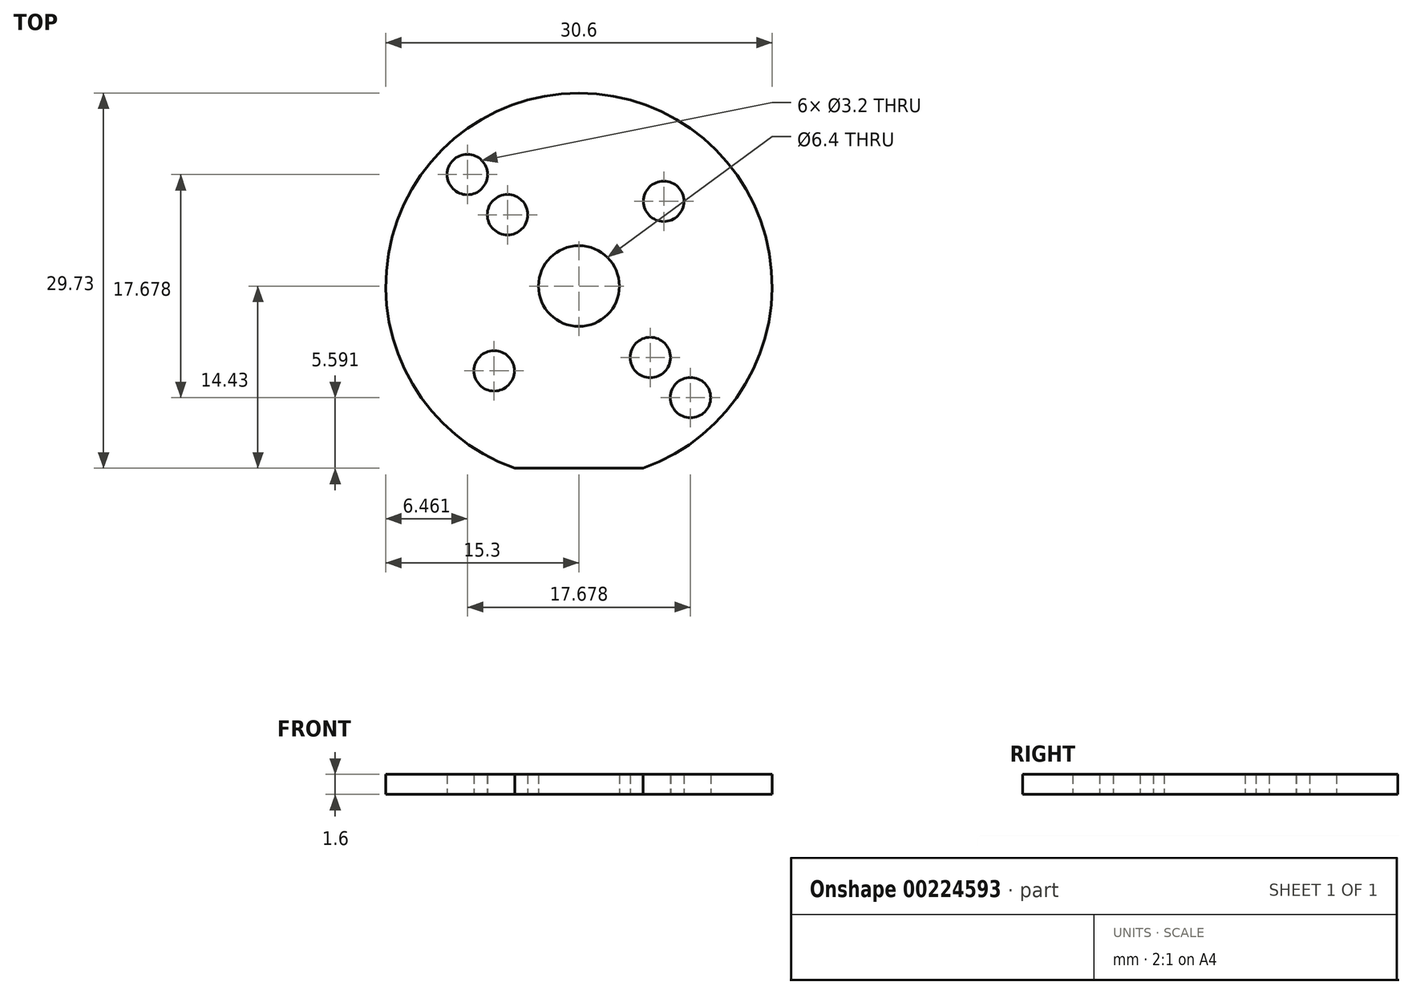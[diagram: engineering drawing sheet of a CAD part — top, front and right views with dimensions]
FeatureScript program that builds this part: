
annotation { "Feature Type Name" : "Feature", "Feature Type Description" : "" }
export const myFeature = defineFeature(function(context is Context, id is Id, definition is map)
    precondition{}
    {
        {
            var Q0;
            Q0=qCreatedBy(makeId("Top.planeOp"),FACE);
            var sketch = newSketch(context, id + "F0", { "sketchPlane" : qUnion([Q0])});
            skLineSegment(sketch, "E0", {"start": v(5.08, -14.43) * mm, "end": v(-5.08, -14.43) * mm});
            skArc(sketch, "E1", {"start": v(5.08, -14.43) * mm, "mid": v(0, 15.3) * mm, "end": v(-5.08, -14.43) * mm});
            skCircle(sketch, "E2", {"center": v(-8.84, 8.84) * mm, "radius": 1.6 * mm});
            skCircle(sketch, "E3", {"center": v(-5.66, 5.66) * mm, "radius": 1.6 * mm});
            skCircle(sketch, "E4", {"center": v(6.72, 6.72) * mm, "radius": 1.6 * mm});
            skCircle(sketch, "E5.MirrorC", {"center": v(5.66, -5.66) * mm, "radius": 1.6 * mm});
            skCircle(sketch, "E6.MirrorC", {"center": v(8.84, -8.84) * mm, "radius": 1.6 * mm});
            skCircle(sketch, "E7.MirrorC", {"center": v(-6.72, -6.72) * mm, "radius": 1.6 * mm});
            skLineSegment(sketch, "E8", {"start": v(-8.84, 8.84) * mm, "end": v(8.84, -8.84) * mm, "construction": true});
            skLineSegment(sketch, "E9", {"start": v(-6.72, -6.72) * mm, "end": v(6.72, 6.72) * mm, "construction": true});
            skCircle(sketch, "E10", {"center": v(0, 0) * mm, "radius": 3.2 * mm});
            skSolve(sketch);
        }
        {
            var Q0;
            Q0 = qSketchRegion(id + "F0", true);
            extrude(context, id + "F1", {"entities" : qUnion([Q0]), "depth" : 1.6 * mm, "offsetDistance" : 25 * mm});
        }
    });
